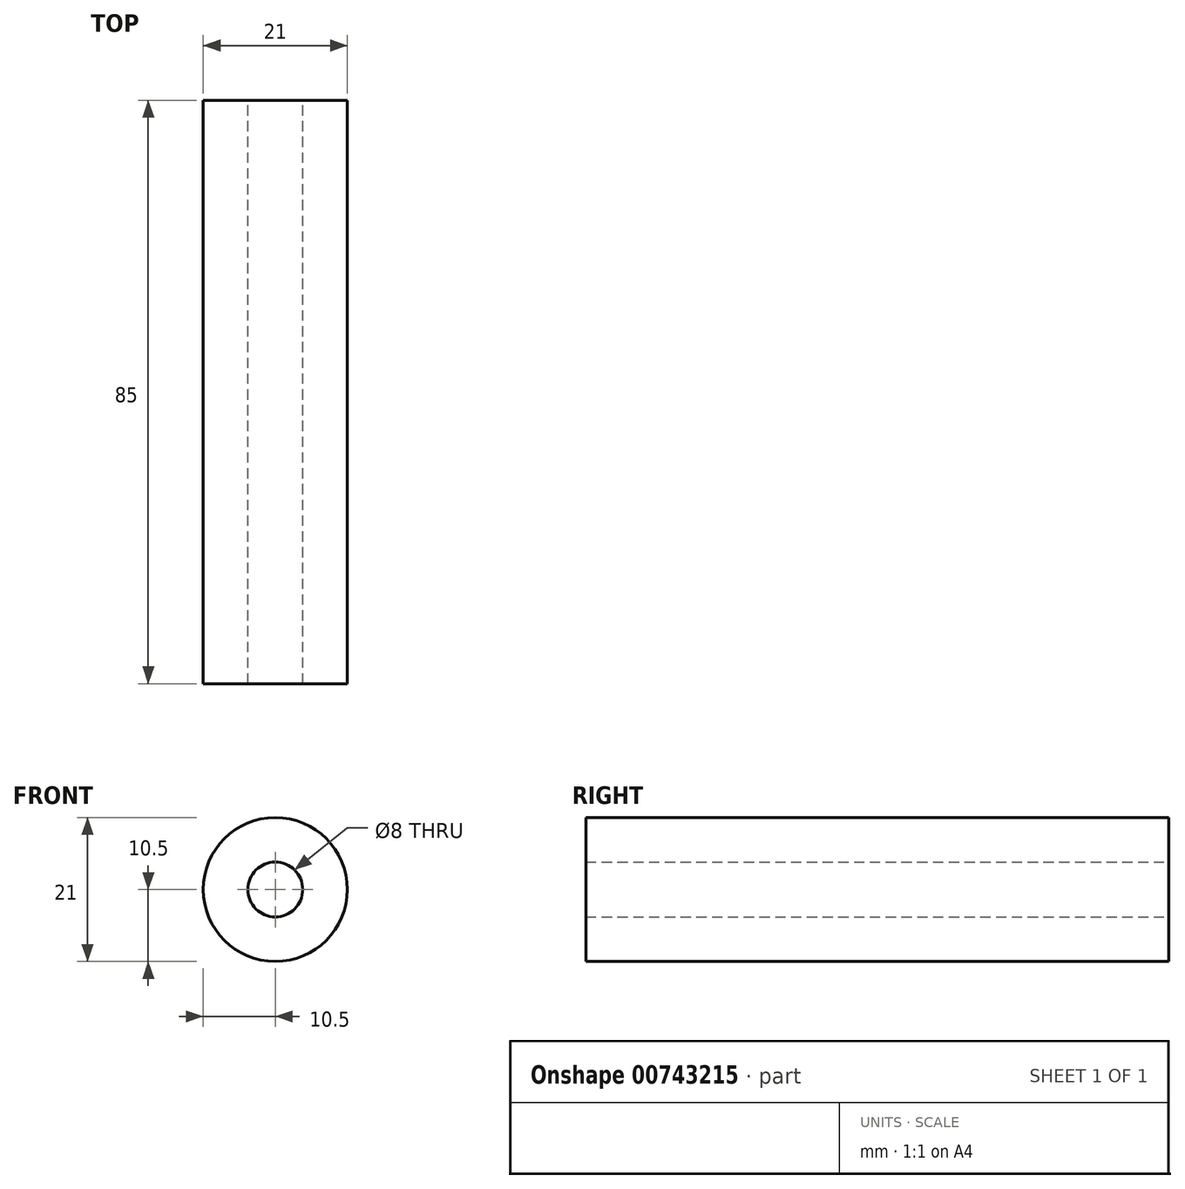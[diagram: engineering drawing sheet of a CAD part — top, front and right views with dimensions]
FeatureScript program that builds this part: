
annotation { "Feature Type Name" : "Feature", "Feature Type Description" : "" }
export const myFeature = defineFeature(function(context is Context, id is Id, definition is map)
    precondition{}
    {
        {
            var Q0;
            Q0=qCreatedBy(makeId("Front.planeOp"),FACE);
            var sketch = newSketch(context, id + "F0", { "sketchPlane" : qUnion([Q0])});
            skCircle(sketch, "E0", {"center": v(0, 0) * mm, "radius": 4 * mm});
            skCircle(sketch, "E1", {"center": v(0, 0) * mm, "radius": 10.5 * mm});
            skSolve(sketch);
        }
        {
            var Q0;
            Q0=makeQuery(id+"F0.imprint","IMPRINT",FACE,{"disambiguationData":[TD([[makeQuery(id+"F0.imprint","IMPRINT",EDGE,{"derivedFrom":sQuery(id+"F0.wireOp",EDGE,"E0")}),-1.0]])]});
            extrude(context, id + "F1", {"entities" : qUnion([Q0]), "depth" : 85 * mm, "offsetDistance" : 25 * mm});
        }
    });
